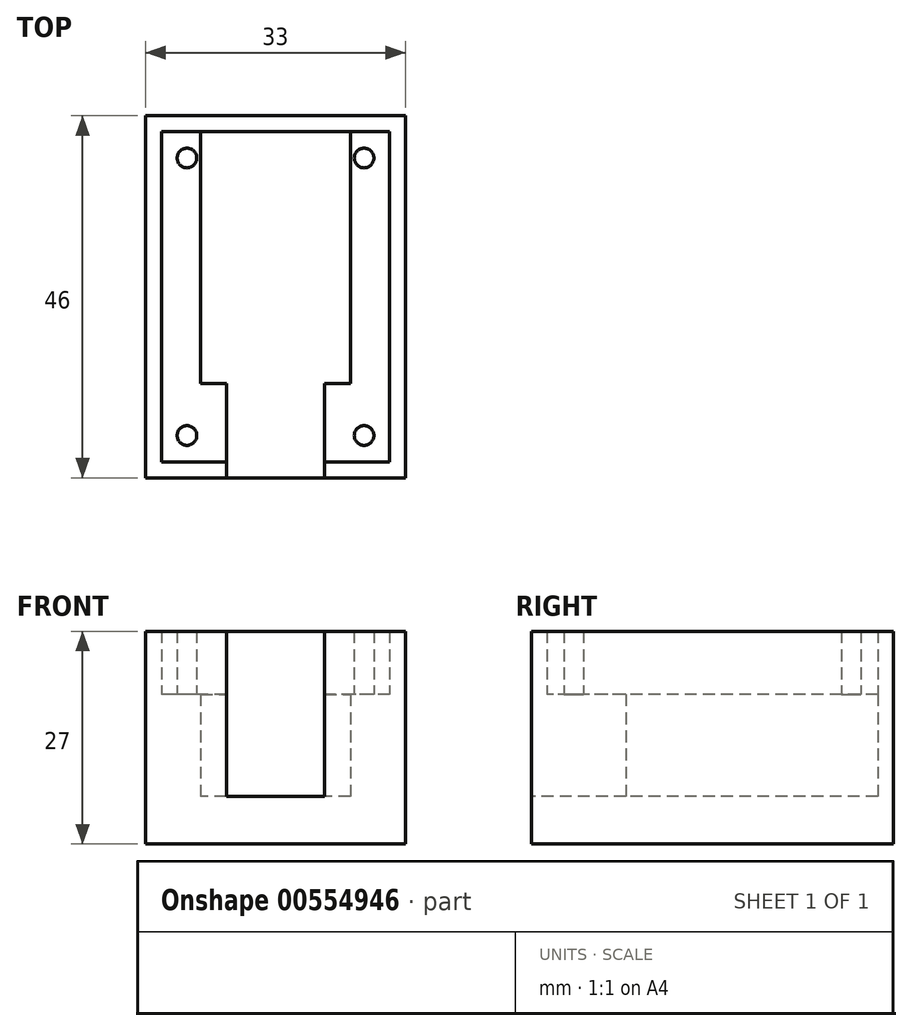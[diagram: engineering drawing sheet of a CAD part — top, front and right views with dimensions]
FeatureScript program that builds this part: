
annotation { "Feature Type Name" : "Feature", "Feature Type Description" : "" }
export const myFeature = defineFeature(function(context is Context, id is Id, definition is map)
    precondition{}
    {
        {
            var Q0;
            Q0=qCreatedBy(makeId("Top.planeOp"),FACE);
            var sketch = newSketch(context, id + "F0", { "sketchPlane" : qUnion([Q0])});
            skLineSegment(sketch, "E0.bottom", {"start": v(14.5, 21) * mm, "end": v(-14.5, 21) * mm});
            skLineSegment(sketch, "E0.top", {"start": v(14.5, -21) * mm, "end": v(-14.5, -21) * mm});
            skLineSegment(sketch, "E0.left", {"start": v(14.5, 21) * mm, "end": v(14.5, -21) * mm});
            skLineSegment(sketch, "E0.right", {"start": v(-14.5, 21) * mm, "end": v(-14.5, -21) * mm});
            skPoint(sketch, "E0.middle", {"position": v(0, 0) * mm});
            skLineSegment(sketch, "E1", {"start": v(-11.25, 17.62) * mm, "end": v(11.25, 17.63) * mm, "construction": true});
            skLineSegment(sketch, "E2", {"start": v(-11.25, 17.62) * mm, "end": v(-11.25, -17.62) * mm, "construction": true});
            skLineSegment(sketch, "E3", {"start": v(-11.25, -17.62) * mm, "end": v(11.25, -17.62) * mm, "construction": true});
            skLineSegment(sketch, "E4", {"start": v(11.25, -17.62) * mm, "end": v(11.25, 17.62) * mm, "construction": true});
            skCircle(sketch, "E5", {"center": v(-11.25, 17.62) * mm, "radius": 1.25 * mm});
            skCircle(sketch, "E6", {"center": v(11.25, 17.62) * mm, "radius": 1.25 * mm});
            skCircle(sketch, "E7", {"center": v(-11.25, -17.62) * mm, "radius": 1.25 * mm});
            skCircle(sketch, "E8", {"center": v(11.25, -17.62) * mm, "radius": 1.25 * mm});
            skLineSegment(sketch, "E9", {"start": v(-16.5, -23) * mm, "end": v(-16.5, 23) * mm});
            skLineSegment(sketch, "E10", {"start": v(-16.5, 23) * mm, "end": v(16.5, 23) * mm});
            skLineSegment(sketch, "E11", {"start": v(16.5, 23) * mm, "end": v(16.5, -23) * mm});
            skLineSegment(sketch, "E12", {"start": v(16.5, -23) * mm, "end": v(-16.5, -23) * mm});
            skLineSegment(sketch, "E13", {"start": v(0, 0) * mm, "end": v(-9.5, 0) * mm, "construction": true});
            skLineSegment(sketch, "E14", {"start": v(-9.5, 0) * mm, "end": v(-9.5, 23) * mm});
            skLineSegment(sketch, "E15", {"start": v(-9.5, 0) * mm, "end": v(-9.5, -23) * mm});
            skLineSegment(sketch, "E16.MirrorCS", {"start": v(9.5, 0) * mm, "end": v(9.5, 23) * mm});
            skLineSegment(sketch, "E17.MirrorCS", {"start": v(9.5, 0) * mm, "end": v(9.5, -23) * mm});
            skLineSegment(sketch, "E18", {"start": v(-9.5, -11) * mm, "end": v(9.5, -11) * mm});
            skLineSegment(sketch, "E19", {"start": v(-6.25, -11) * mm, "end": v(-6.25, -23) * mm});
            skLineSegment(sketch, "E20.MirrorCS", {"start": v(6.25, -11) * mm, "end": v(6.25, -23) * mm});
            skPoint(sketch, "E21", {"position": v(-11.25, 0) * mm});
            skLineSegment(sketch, "E22", {"start": v(-9.5, 0) * mm, "end": v(-11.25, 0) * mm, "construction": true});
            skPoint(sketch, "E23", {"position": v(0, 17.62) * mm});
            skSolve(sketch);
        }
        {
            var Q0;
            {var subQ4=sQuery(id+"F0.wireOp",EDGE,"E0.left");Q0=makeQuery(id+"F0.imprint","IMPRINT",FACE,{"disambiguationData":[TD([[makeQuery(id+"F0.imprint","IMPRINT",EDGE,{"derivedFrom":subQ4}),1.0]])]});}
            var Q1;
            {var subQ0=sQuery(id+"F0.wireOp",EDGE,"E16.MirrorCS");var subQ1=sQuery(id+"F0.wireOp",EDGE,"E0.bottom");var subQ2=makeQuery(id+"F0.imprint","INTERSECT",VERTEX,{"derivedFrom":[subQ1,subQ0]});Q1=makeQuery(id+"F0.imprint","IMPRINT",FACE,{"disambiguationData":[TD([[makeQuery(id+"F0.imprint","IMPRINT",EDGE,{"disambiguationData":[TD([[subQ2,-1.0]])],"derivedFrom":subQ1}),-1.0]])]});}
            var Q2;
            {var subQ0=sQuery(id+"F0.wireOp",EDGE,"E0.left");Q2=makeQuery(id+"F0.imprint","IMPRINT",FACE,{"disambiguationData":[TD([[makeQuery(id+"F0.imprint","IMPRINT",EDGE,{"derivedFrom":subQ0}),-1.0]])]});}
            var Q3;
            {var subQ1=sQuery(id+"F0.wireOp",EDGE,"E16.MirrorCS");var subQ3=sQuery(id+"F0.wireOp",EDGE,"E0.bottom");var subQ4=makeQuery(id+"F0.imprint","INTERSECT",VERTEX,{"derivedFrom":[subQ3,subQ1]});Q3=makeQuery(id+"F0.imprint","IMPRINT",FACE,{"disambiguationData":[TD([[makeQuery(id+"F0.imprint","IMPRINT",EDGE,{"disambiguationData":[TD([[subQ4,-1.0]])],"derivedFrom":subQ3}),1.0]])]});}
            var Q4;
            Q4=makeQuery(id+"F0.imprint","IMPRINT",FACE,{"disambiguationData":[TD([[makeQuery(id+"F0.imprint","IMPRINT",EDGE,{"derivedFrom":sQuery(id+"F0.wireOp",EDGE,"E5")}),1.0]])]});
            var Q5;
            Q5=makeQuery(id+"F0.imprint","IMPRINT",FACE,{"disambiguationData":[TD([[makeQuery(id+"F0.imprint","IMPRINT",EDGE,{"derivedFrom":sQuery(id+"F0.wireOp",EDGE,"E6")}),1.0]])]});
            var Q6;
            Q6=makeQuery(id+"F0.imprint","IMPRINT",FACE,{"disambiguationData":[TD([[makeQuery(id+"F0.imprint","IMPRINT",EDGE,{"derivedFrom":sQuery(id+"F0.wireOp",EDGE,"E7")}),1.0]])]});
            var Q7;
            Q7=makeQuery(id+"F0.imprint","IMPRINT",FACE,{"disambiguationData":[TD([[makeQuery(id+"F0.imprint","IMPRINT",EDGE,{"derivedFrom":sQuery(id+"F0.wireOp",EDGE,"E8")}),1.0]])]});
            var Q8;
            {var subQ6=sQuery(id+"F0.wireOp",EDGE,"E0.right");Q8=makeQuery(id+"F0.imprint","IMPRINT",FACE,{"disambiguationData":[TD([[makeQuery(id+"F0.imprint","IMPRINT",EDGE,{"derivedFrom":subQ6}),-1.0]])]});}
            var Q9;
            {var subQ0=sQuery(id+"F0.wireOp",EDGE,"E17.MirrorCS");var subQ1=sQuery(id+"F0.wireOp",EDGE,"E0.top");var subQ2=makeQuery(id+"F0.imprint","INTERSECT",VERTEX,{"derivedFrom":[subQ1,subQ0]});Q9=makeQuery(id+"F0.imprint","IMPRINT",FACE,{"disambiguationData":[TD([[makeQuery(id+"F0.imprint","IMPRINT",EDGE,{"disambiguationData":[TD([[subQ2,-1.0]])],"derivedFrom":subQ1}),1.0]])]});}
            var Q10;
            {var subQ0=sQuery(id+"F0.wireOp",EDGE,"E0.right");Q10=makeQuery(id+"F0.imprint","IMPRINT",FACE,{"disambiguationData":[TD([[makeQuery(id+"F0.imprint","IMPRINT",EDGE,{"derivedFrom":subQ0}),1.0]])]});}
            var Q11;
            {var subQ0=sQuery(id+"F0.wireOp",EDGE,"E20.MirrorCS");var subQ1=sQuery(id+"F0.wireOp",EDGE,"E0.top");var subQ2=makeQuery(id+"F0.imprint","INTERSECT",VERTEX,{"derivedFrom":[subQ1,subQ0]});Q11=makeQuery(id+"F0.imprint","IMPRINT",FACE,{"disambiguationData":[TD([[makeQuery(id+"F0.imprint","IMPRINT",EDGE,{"disambiguationData":[TD([[subQ2,-1.0]])],"derivedFrom":subQ1}),1.0]])]});}
            var Q12;
            {var subQ0=sQuery(id+"F0.wireOp",EDGE,"E19");var subQ1=sQuery(id+"F0.wireOp",EDGE,"E0.top");var subQ2=makeQuery(id+"F0.imprint","INTERSECT",VERTEX,{"derivedFrom":[subQ1,subQ0]});Q12=makeQuery(id+"F0.imprint","IMPRINT",FACE,{"disambiguationData":[TD([[makeQuery(id+"F0.imprint","IMPRINT",EDGE,{"disambiguationData":[TD([[subQ2,-1.0]])],"derivedFrom":subQ1}),1.0]])]});}
            var Q13;
            {var subQ0=sQuery(id+"F0.wireOp",EDGE,"E17.MirrorCS");var subQ1=sQuery(id+"F0.wireOp",EDGE,"E0.top");var subQ2=makeQuery(id+"F0.imprint","INTERSECT",VERTEX,{"derivedFrom":[subQ1,subQ0]});Q13=makeQuery(id+"F0.imprint","IMPRINT",FACE,{"disambiguationData":[TD([[makeQuery(id+"F0.imprint","IMPRINT",EDGE,{"disambiguationData":[TD([[subQ2,-1.0]])],"derivedFrom":subQ1}),-1.0]])]});}
            var Q14;
            {var subQ0=sQuery(id+"F0.wireOp",EDGE,"E20.MirrorCS");var subQ1=sQuery(id+"F0.wireOp",EDGE,"E0.top");var subQ2=makeQuery(id+"F0.imprint","INTERSECT",VERTEX,{"derivedFrom":[subQ1,subQ0]});Q14=makeQuery(id+"F0.imprint","IMPRINT",FACE,{"disambiguationData":[TD([[makeQuery(id+"F0.imprint","IMPRINT",EDGE,{"disambiguationData":[TD([[subQ2,-1.0]])],"derivedFrom":subQ1}),-1.0]])]});}
            var Q15;
            {var subQ0=sQuery(id+"F0.wireOp",EDGE,"E19");var subQ1=sQuery(id+"F0.wireOp",EDGE,"E0.top");var subQ2=makeQuery(id+"F0.imprint","INTERSECT",VERTEX,{"derivedFrom":[subQ1,subQ0]});Q15=makeQuery(id+"F0.imprint","IMPRINT",FACE,{"disambiguationData":[TD([[makeQuery(id+"F0.imprint","IMPRINT",EDGE,{"disambiguationData":[TD([[subQ2,-1.0]])],"derivedFrom":subQ1}),-1.0]])]});}
            extrude(context, id + "F1", {"entities" : qUnion([Q0, Q1, Q2, Q3, Q4, Q5, Q6, Q7, Q8, Q9, Q10, Q11, Q12, Q13, Q14, Q15]), "depth" : -6 * mm, "offsetDistance" : 25 * mm});
        }
        {
            var Q0;
            {var subQ0=sQuery(id+"F0.wireOp",EDGE,"E0.left");Q0=makeQuery(id+"F0.imprint","IMPRINT",FACE,{"disambiguationData":[TD([[makeQuery(id+"F0.imprint","IMPRINT",EDGE,{"derivedFrom":subQ0}),1.0]])]});}
            var Q1;
            {var subQ0=sQuery(id+"F0.wireOp",EDGE,"E0.right");Q1=makeQuery(id+"F0.imprint","IMPRINT",FACE,{"disambiguationData":[TD([[makeQuery(id+"F0.imprint","IMPRINT",EDGE,{"derivedFrom":subQ0}),-1.0]])]});}
            var Q2;
            Q2=makeQuery(id+"F0.imprint","IMPRINT",FACE,{"disambiguationData":[TD([[makeQuery(id+"F0.imprint","IMPRINT",EDGE,{"derivedFrom":sQuery(id+"F0.wireOp",EDGE,"E8")}),1.0]])]});
            var Q3;
            Q3=makeQuery(id+"F0.imprint","IMPRINT",FACE,{"disambiguationData":[TD([[makeQuery(id+"F0.imprint","IMPRINT",EDGE,{"derivedFrom":sQuery(id+"F0.wireOp",EDGE,"E6")}),1.0]])]});
            var Q4;
            Q4=makeQuery(id+"F0.imprint","IMPRINT",FACE,{"disambiguationData":[TD([[makeQuery(id+"F0.imprint","IMPRINT",EDGE,{"derivedFrom":sQuery(id+"F0.wireOp",EDGE,"E5")}),1.0]])]});
            var Q5;
            Q5=makeQuery(id+"F0.imprint","IMPRINT",FACE,{"disambiguationData":[TD([[makeQuery(id+"F0.imprint","IMPRINT",EDGE,{"derivedFrom":sQuery(id+"F0.wireOp",EDGE,"E7")}),1.0]])]});
            var Q6;
            {var subQ0=sQuery(id+"F0.wireOp",EDGE,"E16.MirrorCS");var subQ1=sQuery(id+"F0.wireOp",EDGE,"E0.bottom");var subQ2=makeQuery(id+"F0.imprint","INTERSECT",VERTEX,{"derivedFrom":[subQ1,subQ0]});Q6=makeQuery(id+"F0.imprint","IMPRINT",FACE,{"disambiguationData":[TD([[makeQuery(id+"F0.imprint","IMPRINT",EDGE,{"disambiguationData":[TD([[subQ2,-1.0]])],"derivedFrom":subQ1}),-1.0]])]});}
            var Q7;
            {var subQ0=sQuery(id+"F0.wireOp",EDGE,"E19");var subQ1=sQuery(id+"F0.wireOp",EDGE,"E0.top");var subQ2=makeQuery(id+"F0.imprint","INTERSECT",VERTEX,{"derivedFrom":[subQ1,subQ0]});Q7=makeQuery(id+"F0.imprint","IMPRINT",FACE,{"disambiguationData":[TD([[makeQuery(id+"F0.imprint","IMPRINT",EDGE,{"disambiguationData":[TD([[subQ2,-1.0]])],"derivedFrom":subQ1}),1.0]])]});}
            var Q8;
            {var subQ0=sQuery(id+"F0.wireOp",EDGE,"E17.MirrorCS");var subQ1=sQuery(id+"F0.wireOp",EDGE,"E0.top");var subQ2=makeQuery(id+"F0.imprint","INTERSECT",VERTEX,{"derivedFrom":[subQ1,subQ0]});Q8=makeQuery(id+"F0.imprint","IMPRINT",FACE,{"disambiguationData":[TD([[makeQuery(id+"F0.imprint","IMPRINT",EDGE,{"disambiguationData":[TD([[subQ2,-1.0]])],"derivedFrom":subQ1}),1.0]])]});}
            extrude(context, id + "F2", {"entities" : qUnion([Q0, Q1, Q2, Q3, Q4, Q5, Q6, Q7, Q8]), "operationType" : NewBodyOperationType.ADD, "depth" : 21 * mm, "offsetDistance" : 25 * mm});
        }
        {
            var Q0;
            {var subQ0=sQuery(id+"F0.wireOp",EDGE,"E0.left");Q0=makeQuery(id+"F0.imprint","IMPRINT",FACE,{"disambiguationData":[TD([[makeQuery(id+"F0.imprint","IMPRINT",EDGE,{"derivedFrom":subQ0}),-1.0]])]});}
            var Q1;
            {var subQ0=sQuery(id+"F0.wireOp",EDGE,"E0.right");Q1=makeQuery(id+"F0.imprint","IMPRINT",FACE,{"disambiguationData":[TD([[makeQuery(id+"F0.imprint","IMPRINT",EDGE,{"derivedFrom":subQ0}),1.0]])]});}
            var Q2;
            {var subQ0=sQuery(id+"F0.wireOp",EDGE,"E19");var subQ1=sQuery(id+"F0.wireOp",EDGE,"E0.top");var subQ2=makeQuery(id+"F0.imprint","INTERSECT",VERTEX,{"derivedFrom":[subQ1,subQ0]});Q2=makeQuery(id+"F0.imprint","IMPRINT",FACE,{"disambiguationData":[TD([[makeQuery(id+"F0.imprint","IMPRINT",EDGE,{"disambiguationData":[TD([[subQ2,-1.0]])],"derivedFrom":subQ1}),-1.0]])]});}
            var Q3;
            {var subQ0=sQuery(id+"F0.wireOp",EDGE,"E19");var subQ1=sQuery(id+"F0.wireOp",EDGE,"E0.top");var subQ2=makeQuery(id+"F0.imprint","INTERSECT",VERTEX,{"derivedFrom":[subQ1,subQ0]});Q3=makeQuery(id+"F0.imprint","IMPRINT",FACE,{"disambiguationData":[TD([[makeQuery(id+"F0.imprint","IMPRINT",EDGE,{"disambiguationData":[TD([[subQ2,-1.0]])],"derivedFrom":subQ1}),1.0]])]});}
            var Q4;
            {var subQ0=sQuery(id+"F0.wireOp",EDGE,"E17.MirrorCS");var subQ1=sQuery(id+"F0.wireOp",EDGE,"E0.top");var subQ2=makeQuery(id+"F0.imprint","INTERSECT",VERTEX,{"derivedFrom":[subQ1,subQ0]});Q4=makeQuery(id+"F0.imprint","IMPRINT",FACE,{"disambiguationData":[TD([[makeQuery(id+"F0.imprint","IMPRINT",EDGE,{"disambiguationData":[TD([[subQ2,-1.0]])],"derivedFrom":subQ1}),1.0]])]});}
            var Q5;
            {var subQ0=sQuery(id+"F0.wireOp",EDGE,"E17.MirrorCS");var subQ1=sQuery(id+"F0.wireOp",EDGE,"E0.top");var subQ2=makeQuery(id+"F0.imprint","INTERSECT",VERTEX,{"derivedFrom":[subQ1,subQ0]});Q5=makeQuery(id+"F0.imprint","IMPRINT",FACE,{"disambiguationData":[TD([[makeQuery(id+"F0.imprint","IMPRINT",EDGE,{"disambiguationData":[TD([[subQ2,-1.0]])],"derivedFrom":subQ1}),-1.0]])]});}
            extrude(context, id + "F3", {"entities" : qUnion([Q0, Q1, Q2, Q3, Q4, Q5]), "operationType" : NewBodyOperationType.ADD, "depth" : 13 * mm, "offsetDistance" : 25 * mm});
        }
    });
